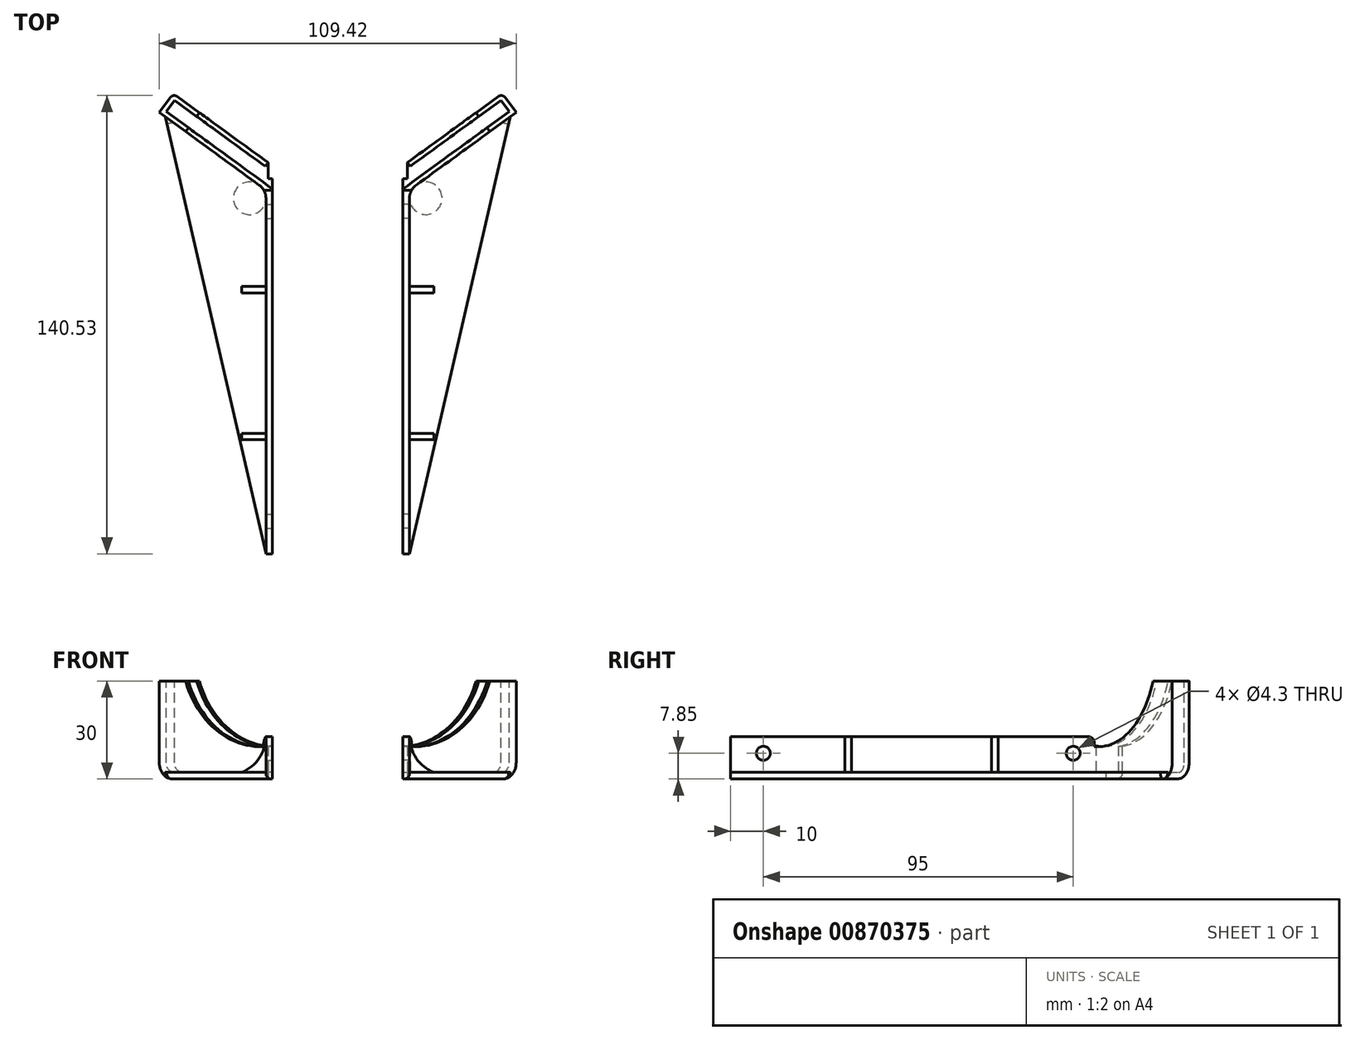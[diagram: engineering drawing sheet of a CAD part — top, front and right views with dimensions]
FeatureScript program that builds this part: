
annotation { "Feature Type Name" : "Feature", "Feature Type Description" : "" }
export const myFeature = defineFeature(function(context is Context, id is Id, definition is map)
    precondition{}
    {
        {
            var Q0;
            Q0=qCreatedBy(makeId("Top.planeOp"),FACE);
            var sketch = newSketch(context, id + "F0", { "sketchPlane" : qUnion([Q0])});
            skLineSegment(sketch, "E0", {"start": v(-20, 115) * mm, "end": v(-20, 0) * mm});
            skLineSegment(sketch, "E1", {"start": v(-20, 0) * mm, "end": v(-22, 0) * mm});
            skLineSegment(sketch, "E2", {"start": v(-20, 115) * mm, "end": v(-21.35, 115) * mm});
            skLineSegment(sketch, "E3", {"start": v(-21.35, 115) * mm, "end": v(-21.35, 120) * mm});
            skLineSegment(sketch, "E4", {"start": v(-21.35, 120) * mm, "end": v(-50.47, 141.16) * mm});
            skLineSegment(sketch, "E5", {"start": v(-50.47, 141.16) * mm, "end": v(-54.59, 135.5) * mm});
            skLineSegment(sketch, "E6", {"start": v(-54.59, 135.5) * mm, "end": v(-52.97, 134.32) * mm});
            skLineSegment(sketch, "E7", {"start": v(-52.97, 134.32) * mm, "end": v(-22, 0) * mm});
            skSolve(sketch);
        }
        {
            var Q0;
            Q0 = qSketchRegion(id + "F0", true);
            extrude(context, id + "F1", {"entities" : qUnion([Q0]), "depth" : 2 * mm, "offsetDistance" : 25 * mm});
        }
        {
            var Q0;
            Q0=makeQuery(id+"F1.opExtrude","SWEPT_FACE",FACE,{"disambiguationData":[OSD([sQuery(id+"F0.wireOp",EDGE,"E0")])]});
            var sketch = newSketch(context, id + "F2", { "sketchPlane" : qUnion([Q0])});
            skLineSegment(sketch, "E8.bottom", {"start": v(0, 0) * mm, "end": v(111.5, 0) * mm});
            skLineSegment(sketch, "E8.top", {"start": v(0, 13) * mm, "end": v(111.5, 13) * mm});
            skLineSegment(sketch, "E8.left", {"start": v(0, 0) * mm, "end": v(0, 13) * mm});
            skLineSegment(sketch, "E8.right", {"start": v(111.5, 0) * mm, "end": v(111.5, 13) * mm});
            skCircle(sketch, "E9", {"center": v(10, 7.85) * mm, "radius": 2.15 * mm});
            skCircle(sketch, "E10", {"center": v(105, 7.85) * mm, "radius": 2.15 * mm});
            skSolve(sketch);
        }
        {
            var Q0;
            Q0 = qSketchRegion(id + "F2", true);
            extrude(context, id + "F3", {"entities" : qUnion([Q0]), "operationType" : NewBodyOperationType.ADD, "oppositeDirection" : true, "depth" : 2 * mm, "offsetDistance" : 25 * mm});
        }
        {
            var Q0;
            Q0=makeQuery(id+"F1.opExtrude","SWEPT_FACE",FACE,{"disambiguationData":[OSD([sQuery(id+"F0.wireOp",EDGE,"E4")])]});
            var sketch = newSketch(context, id + "F4", { "sketchPlane" : qUnion([Q0])});
            skLineSegment(sketch, "E11", {"start": v(87.8, 0) * mm, "end": v(123.8, 0) * mm});
            skLineSegment(sketch, "E12", {"start": v(123.8, 0) * mm, "end": v(123.8, 30) * mm});
            skLineSegment(sketch, "E13", {"start": v(123.8, 30) * mm, "end": v(113.8, 30) * mm});
            skArc(sketch, "E14", {"start": v(87.8, 10) * mm, "mid": v(103.78, 16.13) * mm, "end": v(113.8, 30) * mm});
            skLineSegment(sketch, "E15", {"start": v(87.8, 0) * mm, "end": v(87.8, 10) * mm});
            skSolve(sketch);
        }
        {
            var Q0;
            Q0 = qSketchRegion(id + "F4", true);
            extrude(context, id + "F5", {"entities" : qUnion([Q0]), "operationType" : NewBodyOperationType.ADD, "oppositeDirection" : true, "depth" : 7.2 * mm, "offsetDistance" : 25 * mm});
        }
        {
            var Q0;
            Q0=makeQuery(id+"F5.boolean.opBoolean","MERGE",FACE,{"derivedFrom":[makeQuery(id+"F1.opExtrude","SWEPT_FACE",FACE,{"disambiguationData":[OSD([sQuery(id+"F0.wireOp",EDGE,"E4")])]}),makeQuery(id+"F5.opExtrude","CAP_FACE",FACE,{"disambiguationData":[OSD([sQuery(id+"F4.wireOp",EDGE,"E11"),sQuery(id+"F4.wireOp",EDGE,"E12"),sQuery(id+"F4.wireOp",EDGE,"E13"),sQuery(id+"F4.wireOp",EDGE,"E14"),sQuery(id+"F4.wireOp",EDGE,"E15")])],"isStart":true})]});
            var Q1;
            Q1=makeQuery(id+"F5.opExtrude","CAP_FACE",FACE,{"disambiguationData":[OSD([sQuery(id+"F4.wireOp",EDGE,"E11"),sQuery(id+"F4.wireOp",EDGE,"E12"),sQuery(id+"F4.wireOp",EDGE,"E13"),sQuery(id+"F4.wireOp",EDGE,"E14"),sQuery(id+"F4.wireOp",EDGE,"E15")])],"isStart":false});
            cPlane(context, id + "F6", {"entities" : qUnion([Q0, Q1]), "cplaneType" : CPlaneType.MID_PLANE, "offset" : 25 * mm, "width" : 150 * mm, "height" : 150 * mm});
        }
        {
            var Q0;
            Q0=qCreatedBy(id+"F6.planeOp",FACE);
            var sketch = newSketch(context, id + "F7", { "sketchPlane" : qUnion([Q0])});
            skLineSegment(sketch, "E16.0", {"start": v(84.87, 2) * mm, "end": v(87.8, 2) * mm});
            skLineSegment(sketch, "E17", {"start": v(87.8, 2) * mm, "end": v(119.2, 2) * mm});
            skArc(sketch, "E18", {"start": v(119.2, 2) * mm, "mid": v(121.33, 2.88) * mm, "end": v(122.2, 5) * mm});
            skLineSegment(sketch, "E19.0", {"start": v(123.8, 30) * mm, "end": v(113.8, 30) * mm});
            skLineSegment(sketch, "E20", {"start": v(122.2, 5) * mm, "end": v(122.2, 30) * mm});
            skLineSegment(sketch, "E21", {"start": v(122.2, 30) * mm, "end": v(87.8, 30) * mm});
            skLineSegment(sketch, "E22", {"start": v(87.8, 30) * mm, "end": v(87.8, 2) * mm});
            skSolve(sketch);
        }
        {
            var Q0;
            Q0 = qSketchRegion(id + "F7", true);
            extrude(context, id + "F8", {"entities" : qUnion([Q0]), "operationType" : NewBodyOperationType.REMOVE, "oppositeDirection" : true, "depth" : 4.3 * mm, "offsetDistance" : 25 * mm, "symmetric" : true});
        }
        {
            var Q0;
            Q0=makeQuery(id+"F5.boolean.opBoolean","MERGE",EDGE,{"derivedFrom":[makeQuery(id+"F1.opExtrude","CAP_EDGE",EDGE,{"disambiguationData":[OSD([sQuery(id+"F0.wireOp",EDGE,"E5")])],"isStart":true}),makeQuery(id+"F5.opExtrude","SWEPT_EDGE",EDGE,{"disambiguationData":[OSD([sQuery(id+"F4.wireOp",EDGE,"E11"),sQuery(id+"F4.wireOp",EDGE,"E12")])]})]});
            fillet(context, id + "F9", {"entities" : qUnion([Q0]), "radius" : 5 * mm, "tangentPropagation" : true, "allowEdgeOverflow" : false});
        }
        {
            var Q0;
            {var subQ0=sQuery(id+"F4.wireOp",EDGE,"E12");var subQ1=sQuery(id+"F4.wireOp",EDGE,"E11");Q0=makeQuery(id+"F9.opFillet","BLEND_EDGE",EDGE,{"blendedFrom":[makeQuery(id+"F5.boolean.opBoolean","MERGE",EDGE,{"derivedFrom":[makeQuery(id+"F1.opExtrude","CAP_EDGE",EDGE,{"disambiguationData":[OSD([sQuery(id+"F0.wireOp",EDGE,"E5")])],"isStart":true}),makeQuery(id+"F5.opExtrude","SWEPT_EDGE",EDGE,{"disambiguationData":[OSD([subQ1,subQ0])]})]}),makeQuery(id+"F5.boolean.opBoolean","MERGE",FACE,{"derivedFrom":[makeQuery(id+"F1.opExtrude","SWEPT_FACE",FACE,{"disambiguationData":[OSD([sQuery(id+"F0.wireOp",EDGE,"E4")])]}),makeQuery(id+"F5.opExtrude","CAP_FACE",FACE,{"disambiguationData":[OSD([subQ1,subQ0,sQuery(id+"F4.wireOp",EDGE,"E13"),sQuery(id+"F4.wireOp",EDGE,"E14"),sQuery(id+"F4.wireOp",EDGE,"E15")])],"isStart":true})]})],"blendedInto":[makeQuery(id+"F5.boolean.opBoolean","MERGE",FACE,{"derivedFrom":[makeQuery(id+"F1.opExtrude","SWEPT_FACE",FACE,{"disambiguationData":[OSD([sQuery(id+"F0.wireOp",EDGE,"E4")])]}),makeQuery(id+"F5.opExtrude","CAP_FACE",FACE,{"disambiguationData":[OSD([subQ1,subQ0,sQuery(id+"F4.wireOp",EDGE,"E13"),sQuery(id+"F4.wireOp",EDGE,"E14"),sQuery(id+"F4.wireOp",EDGE,"E15")])],"isStart":true})]})]});}
            var Q1;
            Q1=makeQuery(id+"F1.opExtrude","CAP_EDGE",EDGE,{"disambiguationData":[OSD([sQuery(id+"F0.wireOp",EDGE,"E7")])],"isStart":true});
            fillet(context, id + "F10", {"entities" : qUnion([Q0, Q1]), "radius" : 1.6 * mm, "tangentPropagation" : true, "allowEdgeOverflow" : false});
        }
        {
            var Q0;
            Q0=qCreatedBy(makeId("Front.planeOp"),FACE);
            cPlane(context, id + "F11", {"entities" : qUnion([Q0]), "cplaneType" : CPlaneType.OFFSET, "offset" : 35 * mm, "oppositeDirection" : true, "width" : 150 * mm, "height" : 150 * mm});
        }
        {
            var Q0;
            Q0=qCreatedBy(id+"F11.planeOp",FACE);
            var sketch = newSketch(context, id + "F12", { "sketchPlane" : qUnion([Q0])});
            skLineSegment(sketch, "E23.0", {"start": v(-22, 13) * mm, "end": v(-22, 2) * mm});
            skArc(sketch, "E24", {"start": v(-29.5, 2) * mm, "mid": v(-24.05, 6.34) * mm, "end": v(-22, 13) * mm});
            skLineSegment(sketch, "E25", {"start": v(-22, 2) * mm, "end": v(-29.5, 2) * mm});
            skSolve(sketch);
        }
        {
            var Q0;
            Q0 = qSketchRegion(id + "F12", true);
            extrude(context, id + "F13", {"entities" : qUnion([Q0]), "operationType" : NewBodyOperationType.ADD, "oppositeDirection" : true, "depth" : 2 * mm, "offsetDistance" : 25 * mm});
        }
        {
            var Q0;
            Q0=qCreatedBy(id+"F11.planeOp",FACE);
            cPlane(context, id + "F14", {"entities" : qUnion([Q0]), "cplaneType" : CPlaneType.OFFSET, "offset" : 45 * mm, "oppositeDirection" : true, "width" : 150 * mm, "height" : 150 * mm});
        }
        {
            var Q0;
            Q0=qCreatedBy(id+"F14.planeOp",FACE);
            var sketch = newSketch(context, id + "F15", { "sketchPlane" : qUnion([Q0])});
            skArc(sketch, "E26.0", {"start": v(-29.5, 2) * mm, "mid": v(-24.05, 6.34) * mm, "end": v(-22, 13) * mm});
            skLineSegment(sketch, "E27.0", {"start": v(-22, 13) * mm, "end": v(-22, 2) * mm});
            skLineSegment(sketch, "E28", {"start": v(-22, 2) * mm, "end": v(-29.5, 2) * mm});
            skSolve(sketch);
        }
        {
            var Q0;
            Q0 = qSketchRegion(id + "F15", true);
            extrude(context, id + "F16", {"entities" : qUnion([Q0]), "operationType" : NewBodyOperationType.ADD, "oppositeDirection" : true, "depth" : 2 * mm, "offsetDistance" : 25 * mm});
        }
        {
            var Q0;
            Q0=makeQuery(id+"F3.opExtrude","SWEPT_EDGE",EDGE,{"disambiguationData":[OSD([sQuery(id+"F2.wireOp",EDGE,"E8.top"),sQuery(id+"F2.wireOp",EDGE,"E8.right")])]});
            fillet(context, id + "F17", {"entities" : qUnion([Q0]), "tangentPropagation" : true, "radius" : 2 * mm, "defaultsChanged" : true, "vertexSettings" : [], "allowEdgeOverflow" : false});
        }
        {
            var Q0;
            Q0=makeQuery(id+"F8.boolean.opBoolean","MERGE",FACE,{"derivedFrom":[makeQuery(id+"F1.opExtrude","CAP_FACE",FACE,{"disambiguationData":[OSD([sQuery(id+"F0.wireOp",EDGE,"E0"),sQuery(id+"F0.wireOp",EDGE,"E1"),sQuery(id+"F0.wireOp",EDGE,"E2"),sQuery(id+"F0.wireOp",EDGE,"E3"),sQuery(id+"F0.wireOp",EDGE,"E4"),sQuery(id+"F0.wireOp",EDGE,"E5"),sQuery(id+"F0.wireOp",EDGE,"E6"),sQuery(id+"F0.wireOp",EDGE,"E7")])],"isStart":false})],"fromTools":[makeQuery(id+"F8.opExtrude","SWEPT_FACE",FACE,{"disambiguationData":[OSD([sQuery(id+"F7.wireOp",EDGE,"E17")])]})]});
            var sketch = newSketch(context, id + "F18", { "sketchPlane" : qUnion([Q0])});
            skLineSegment(sketch, "E29", {"start": v(-24.73, 115.35) * mm, "end": v(-20, 111.91) * mm});
            skLineSegment(sketch, "E30", {"start": v(-20, 111.91) * mm, "end": v(-20, 111.5) * mm});
            skLineSegment(sketch, "E31", {"start": v(-20, 111.5) * mm, "end": v(-22, 111.5) * mm});
            skLineSegment(sketch, "E32", {"start": v(-24.73, 115.35) * mm, "end": v(-25.58, 114.18) * mm});
            skLineSegment(sketch, "E33", {"start": v(-25.58, 114.18) * mm, "end": v(-22, 111.57) * mm});
            skLineSegment(sketch, "E34", {"start": v(-22, 111.57) * mm, "end": v(-22, 111.5) * mm});
            skSolve(sketch);
        }
        {
            var Q0;
            Q0 = qSketchRegion(id + "F18", true);
            var Q1;
            {var subQ0=sQuery(id+"F4.wireOp",EDGE,"E15");var subQ1=sQuery(id+"F4.wireOp",EDGE,"E14");var subQ2=sQuery(id+"F4.wireOp",EDGE,"E13");Q1=makeQuery(id+"F8.boolean.opBoolean","SPLIT",FACE,{"disambiguationData":[TD([makeQuery(id+"F5.opExtrude","CAP_FACE",FACE,{"disambiguationData":[OSD([sQuery(id+"F4.wireOp",EDGE,"E11"),sQuery(id+"F4.wireOp",EDGE,"E12"),subQ2,subQ1,subQ0])],"isStart":false})])],"derivedFrom":makeQuery(id+"F5.opExtrude","SWEPT_FACE",FACE,{"disambiguationData":[OSD([subQ1])]})});}
            extrude(context, id + "F19", {"entities" : qUnion([Q0]), "operationType" : NewBodyOperationType.ADD, "endBound" : BoundingType.UP_TO_SURFACE, "depth" : 25 * mm, "endBoundEntityFace" : qUnion([Q1]), "offsetDistance" : 25 * mm});
        }
        {
            var Q0;
            Q0=makeQuery(id+"F19.opExtrude","SWEPT_EDGE",EDGE,{"disambiguationData":[OSD([sQuery(id+"F18.wireOp",EDGE,"E33"),sQuery(id+"F18.wireOp",EDGE,"E34")])]});
            fillet(context, id + "F20", {"entities" : qUnion([Q0]), "tangentPropagation" : true, "radius" : 5 * mm, "defaultsChanged" : false, "vertexSettings" : [], "allowEdgeOverflow" : false});
        }
        {
            var Q0;
            Q0=makeQuery(id+"F1.opExtrude","SWEPT_BODY",BODY,{"disambiguationData":[OSD([sQuery(id+"F0.wireOp",EDGE,"E0"),sQuery(id+"F0.wireOp",EDGE,"E1"),sQuery(id+"F0.wireOp",EDGE,"E2"),sQuery(id+"F0.wireOp",EDGE,"E3"),sQuery(id+"F0.wireOp",EDGE,"E4"),sQuery(id+"F0.wireOp",EDGE,"E5"),sQuery(id+"F0.wireOp",EDGE,"E6"),sQuery(id+"F0.wireOp",EDGE,"E7")])]});
            var Q1;
            Q1=qCreatedBy(makeId("Right.planeOp"),FACE);
            mirror(context, id + "F21", {"entities" : qUnion([Q0]), "mirrorPlane" : qUnion([Q1])});
        }
    });
